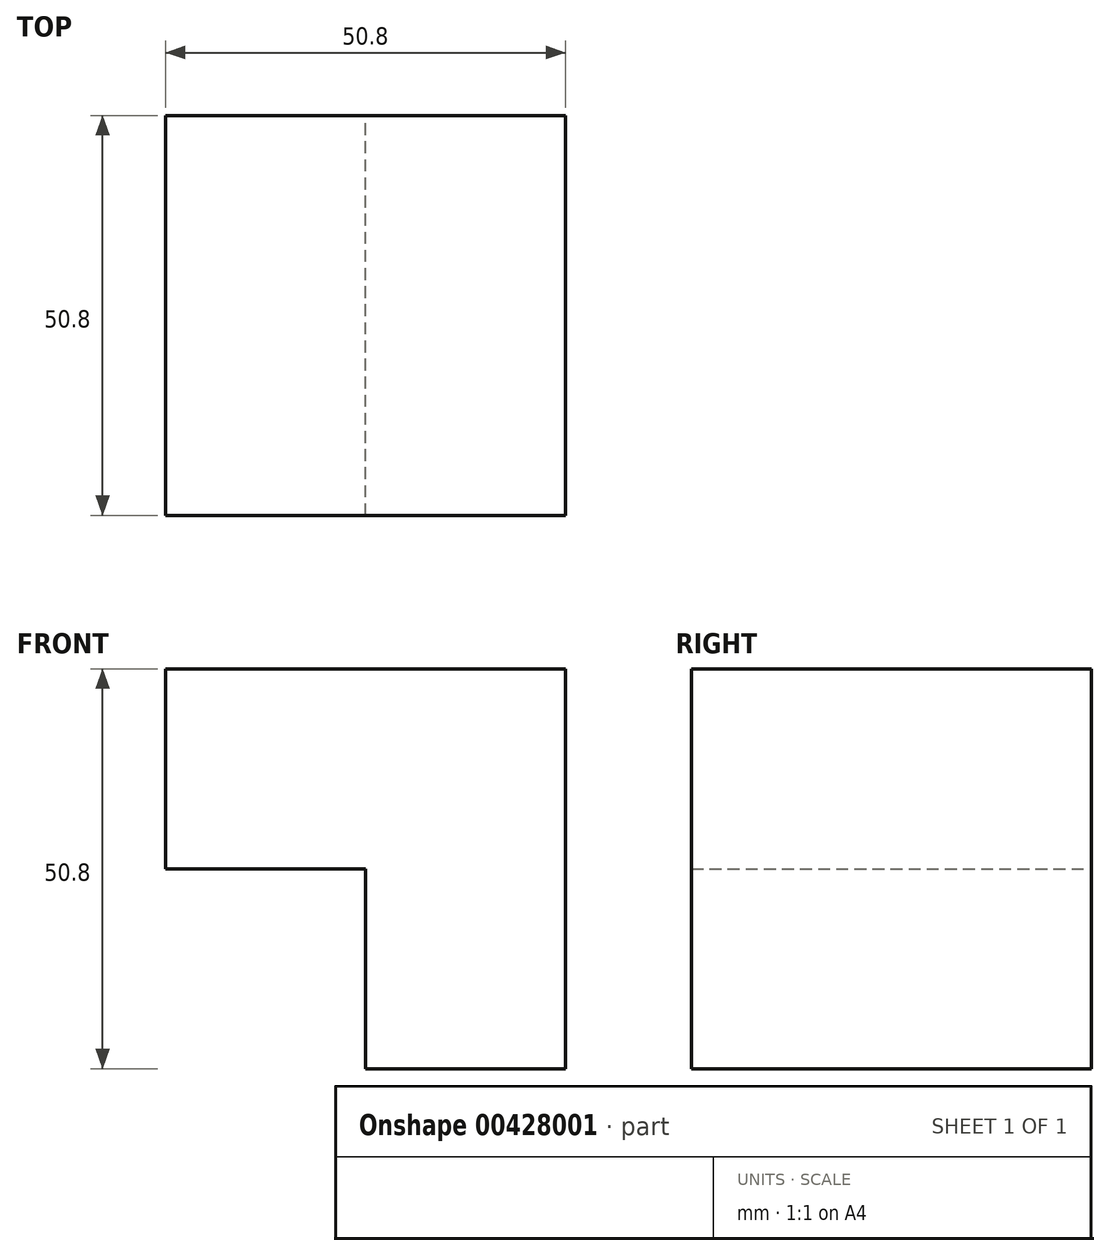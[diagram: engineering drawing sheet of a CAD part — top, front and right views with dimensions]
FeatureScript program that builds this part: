
annotation { "Feature Type Name" : "Feature", "Feature Type Description" : "" }
export const myFeature = defineFeature(function(context is Context, id is Id, definition is map)
    precondition{}
    {
        {
            var Q0;
            Q0=qCreatedBy(makeId("Front.planeOp"),FACE);
            var sketch = newSketch(context, id + "F0", { "sketchPlane" : qUnion([Q0])});
            skLineSegment(sketch, "E0.bottom", {"start": v(0, 0) * mm, "end": v(-25.4, 0) * mm});
            skLineSegment(sketch, "E0.top", {"start": v(0, 50.8) * mm, "end": v(-50.8, 50.8) * mm});
            skLineSegment(sketch, "E0.left", {"start": v(0, 0) * mm, "end": v(0, 50.8) * mm});
            skLineSegment(sketch, "E0.right", {"start": v(-50.8, 25.4) * mm, "end": v(-50.8, 50.8) * mm});
            skLineSegment(sketch, "E1", {"start": v(-50.8, 25.4) * mm, "end": v(-25.4, 25.4) * mm});
            skLineSegment(sketch, "E2", {"start": v(-25.4, 25.4) * mm, "end": v(-25.4, 0) * mm});
            skPoint(sketch, "E3.orphan", {"position": v(-50.8, 0) * mm});
            skSolve(sketch);
        }
        {
            var Q0;
            Q0 = qSketchRegion(id + "F0", true);
            extrude(context, id + "F1", {"entities" : qUnion([Q0]), "depth" : 50.8 * mm});
        }
    });
